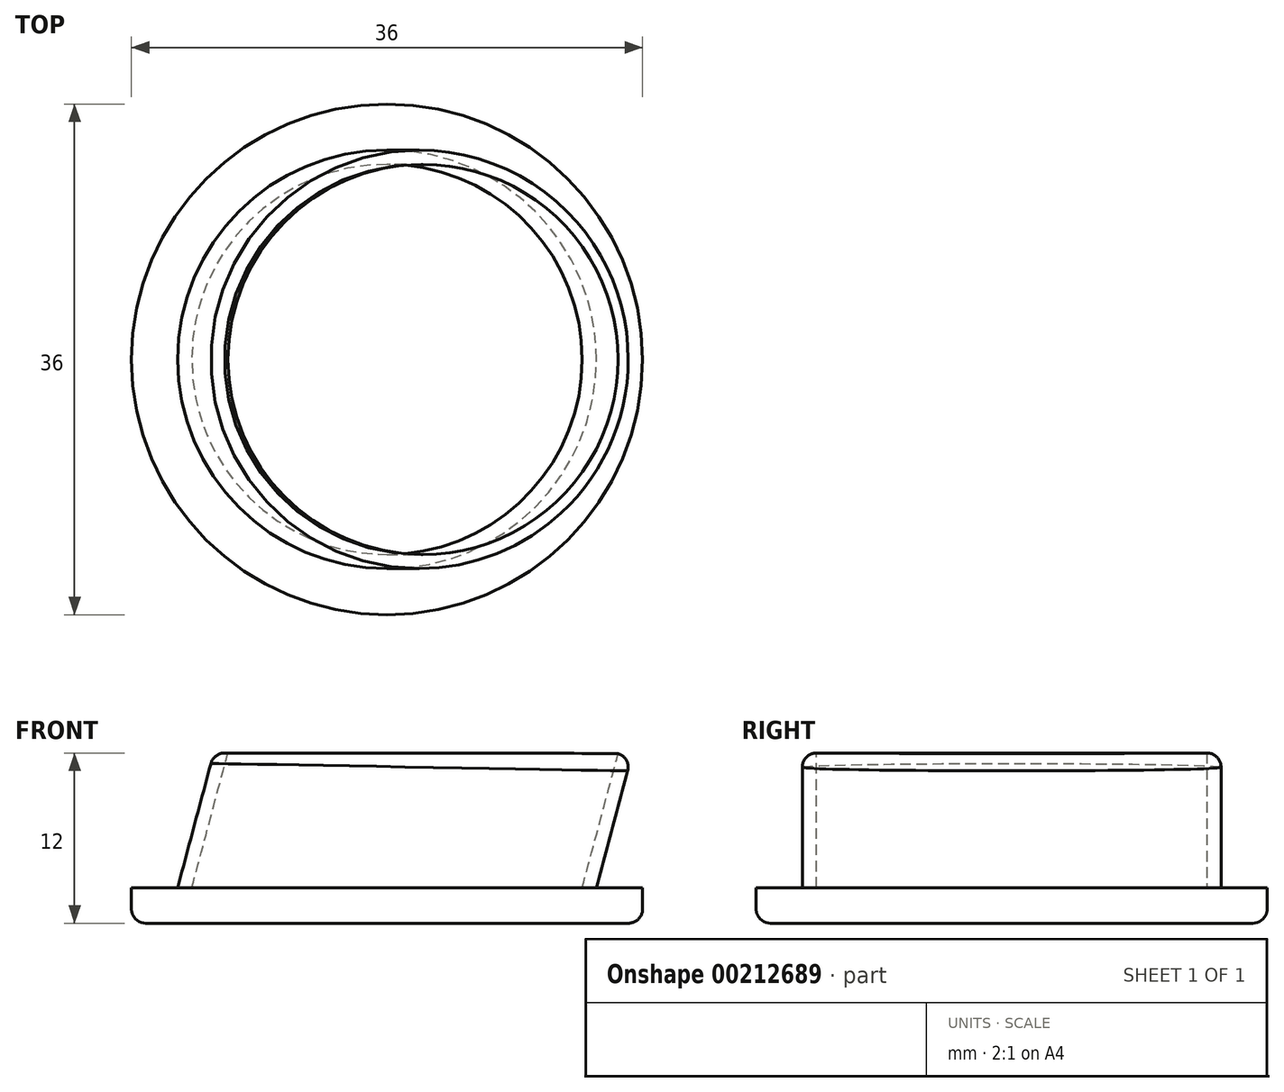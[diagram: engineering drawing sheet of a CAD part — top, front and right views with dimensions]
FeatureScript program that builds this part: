
annotation { "Feature Type Name" : "Feature", "Feature Type Description" : "" }
export const myFeature = defineFeature(function(context is Context, id is Id, definition is map)
    precondition{}
    {
        {
            var Q0;
            Q0=qCreatedBy(makeId("Front.planeOp"),FACE);
            var sketch = newSketch(context, id + "F0", { "sketchPlane" : qUnion([Q0])});
            skLineSegment(sketch, "E0", {"start": v(0, 0) * mm, "end": v(18, 0) * mm});
            skLineSegment(sketch, "E1", {"start": v(0, 0) * mm, "end": v(-18, 0) * mm});
            skLineSegment(sketch, "E2", {"start": v(0, 0) * mm, "end": v(0, 12) * mm});
            skLineSegment(sketch, "E3", {"start": v(0, 0) * mm, "end": v(0, 2.5) * mm});
            skLineSegment(sketch, "E4", {"start": v(0, 2.5) * mm, "end": v(2.55, 12) * mm, "construction": true});
            skLineSegment(sketch, "E5", {"start": v(0, 12) * mm, "end": v(9.3, 12) * mm, "construction": true});
            skLineSegment(sketch, "E6", {"start": v(2.55, 12) * mm, "end": v(6.6, 27.14) * mm, "construction": true});
            skLineSegment(sketch, "E7", {"start": v(0, 12) * mm, "end": v(0, 22) * mm, "construction": true});
            skLineSegment(sketch, "E8", {"start": v(0, 22) * mm, "end": v(5.23, 22) * mm, "construction": true});
            skSolve(sketch);
        }
        {
            var Q0;
            Q0=qCreatedBy(makeId("Top.planeOp"),FACE);
            var sketch = newSketch(context, id + "F1", { "sketchPlane" : qUnion([Q0])});
            skCircle(sketch, "E9", {"center": v(0, 0) * mm, "radius": 18 * mm});
            skCircle(sketch, "E10", {"center": v(0, 0) * mm, "radius": 14.75 * mm});
            skCircle(sketch, "E11", {"center": v(0, 0) * mm, "radius": 13.75 * mm});
            skSolve(sketch);
        }
        {
            var Q0;
            Q0=makeQuery(id+"F1.imprint","IMPRINT",FACE,{"disambiguationData":[TD([[makeQuery(id+"F1.imprint","IMPRINT",EDGE,{"derivedFrom":sQuery(id+"F1.wireOp",EDGE,"E9")}),1.0]])]});
            var Q1;
            Q1=makeQuery(id+"F1.imprint","IMPRINT",FACE,{"disambiguationData":[TD([[makeQuery(id+"F1.imprint","IMPRINT",EDGE,{"derivedFrom":sQuery(id+"F1.wireOp",EDGE,"E10")}),1.0]])]});
            var Q2;
            Q2=makeQuery(id+"F1.imprint","IMPRINT",FACE,{"disambiguationData":[TD([[makeQuery(id+"F1.imprint","IMPRINT",EDGE,{"derivedFrom":sQuery(id+"F1.wireOp",EDGE,"E11")}),1.0]])]});
            extrude(context, id + "F2", {"entities" : qUnion([Q0, Q1, Q2]), "depth" : 2.5 * mm});
        }
        {
            var Q0;
            Q0=makeQuery(id+"F2.opExtrude","CAP_FACE",FACE,{"disambiguationData":[OSD([sQuery(id+"F1.wireOp",EDGE,"E9")])],"isStart":true});
            fillet(context, id + "F3", {"entities" : qUnion([Q0]), "radius" : 1 * mm, "tangentPropagation" : true, "allowEdgeOverflow" : false});
        }
        {
            var Q0;
            Q0=makeQuery(id+"F2.opExtrude","CAP_FACE",FACE,{"disambiguationData":[OSD([sQuery(id+"F1.wireOp",EDGE,"E9")])],"isStart":false});
            var sketch = newSketch(context, id + "F4", { "sketchPlane" : qUnion([Q0])});
            skCircle(sketch, "E12.0", {"center": v(0, 0) * mm, "radius": 14.75 * mm});
            skSolve(sketch);
        }
        {
            var Q0;
            Q0=makeQuery(id+"F4.imprint","IMPRINT",FACE,{"disambiguationData":[TD([[makeQuery(id+"F4.imprint","IMPRINT",EDGE,{"derivedFrom":sQuery(id+"F4.wireOp",EDGE,"E12.0")}),1.0]])]});
            cPlane(context, id + "F5", {"entities" : qUnion([Q0]), "cplaneType" : CPlaneType.OFFSET, "offset" : 9.5 * mm, "width" : 150 * mm, "height" : 150 * mm});
        }
        {
            var Q0;
            Q0=qCreatedBy(id+"F5.planeOp",FACE);
            var sketch = newSketch(context, id + "F6", { "sketchPlane" : qUnion([Q0])});
            skPoint(sketch, "E13.0", {"position": v(2.55, 0) * mm});
            skLineSegment(sketch, "E14.0", {"start": v(0, 0) * mm, "end": v(2.55, 0) * mm});
            skCircle(sketch, "E15", {"center": v(2.55, 0) * mm, "radius": 14.75 * mm});
            skSolve(sketch);
        }
        {
            var Q1;
            Q1=makeQuery(id+"F4.imprint","IMPRINT",FACE,{"disambiguationData":[TD([[makeQuery(id+"F4.imprint","IMPRINT",EDGE,{"derivedFrom":sQuery(id+"F4.wireOp",EDGE,"E12.0")}),1.0]])]});
            var Q2;
            Q2=makeQuery(id+"F6.imprint","IMPRINT",FACE,{"disambiguationData":[TD([[makeQuery(id+"F6.imprint","IMPRINT",EDGE,{"derivedFrom":sQuery(id+"F6.wireOp",EDGE,"E15")}),1.0]])]});
            loft(context, id + "F7", {"operationType" : NewBodyOperationType.ADD, "sheetProfilesArray" : [{ "sheetProfileEntities" : qUnion([Q1]) }, { "sheetProfileEntities" : qUnion([Q2]) }]});
        }
        {
            var Q0;
            Q0=makeQuery(id+"F6.imprint","IMPRINT",FACE,{"disambiguationData":[TD([[makeQuery(id+"F6.imprint","IMPRINT",EDGE,{"derivedFrom":sQuery(id+"F6.wireOp",EDGE,"E15")}),1.0]])]});
            var sketch = newSketch(context, id + "F8", { "sketchPlane" : qUnion([Q0])});
            skPoint(sketch, "E16.0", {"position": v(2.55, 0) * mm});
            skCircle(sketch, "E17", {"center": v(2.55, 0) * mm, "radius": 13.75 * mm});
            skSolve(sketch);
        }
        {
            var Q0;
            Q0=qCreatedBy(id+"F5.planeOp",FACE);
            cPlane(context, id + "F9", {"entities" : qUnion([Q0]), "cplaneType" : CPlaneType.OFFSET, "offset" : 9.5 * mm, "oppositeDirection" : true, "width" : 150 * mm, "height" : 150 * mm});
        }
        {
            var Q0;
            Q0=qCreatedBy(id+"F9.planeOp",FACE);
            var sketch = newSketch(context, id + "F10", { "sketchPlane" : qUnion([Q0])});
            skPoint(sketch, "E18.0", {"position": v(0, 0) * mm});
            skCircle(sketch, "E19", {"center": v(0, 0) * mm, "radius": 13.75 * mm});
            skSolve(sketch);
        }
        {
            var Q1;
            Q1 = qSketchRegion(id + "F10", true);
            var Q2;
            Q2 = qSketchRegion(id + "F8", true);
            loft(context, id + "F11", {"operationType" : NewBodyOperationType.REMOVE, "sheetProfilesArray" : [{ "sheetProfileEntities" : qUnion([Q1]) }, { "sheetProfileEntities" : qUnion([Q2]) }]});
        }
        {
            var Q0;
            Q0=makeQuery(id+"F7.opLoft","MID_CAP_EDGE",EDGE,{"disambiguationData":[OSD([sQuery(id+"F4.wireOp",EDGE,"E12.0"),sQuery(id+"F6.wireOp",EDGE,"E15")])],"capPos":1.0});
            fillet(context, id + "F12", {"entities" : qUnion([Q0]), "radius" : 1 * mm, "tangentPropagation" : true, "allowEdgeOverflow" : false});
        }
    });
